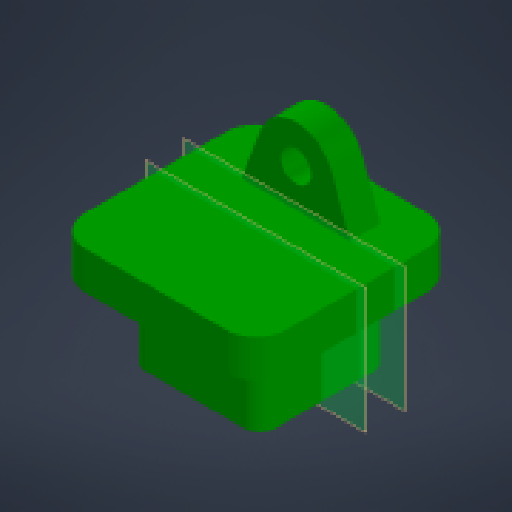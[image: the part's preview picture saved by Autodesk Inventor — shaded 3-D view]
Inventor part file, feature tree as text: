
AUTODESK INVENTOR PART (.ipt)
format: ipt  version: 2024 (Build 280153000, 153)  size: 190,464 bytes
history: native  units: mm
features: other x8, reference x8, extrude x3, sketch x3, fillet x2
ambient origin geometry x8: Origin, YZ Plane, XZ Plane, XY Plane, X Axis, Y Axis, Z Axis, Center Point
bodies: Body1 (feature_tree)
feature tree (24):
  other  "Твердое тело1"
  extrude  "Выдавливание1"  Depth=2.0mm
  extrude  "Выдавливание2"  Depth=10.0mm TaperAngle=0.0deg
  fillet  "Сопряжение1"  Radius=5.0mm
  fillet  "Сопряжение2"  Radius=2.0mm
  other  "РабПлоскость2"
  extrude  "Выдавливание3"  Depth=4.0mm
  sketch  "Эскиз1"
  reference  "Ссылка1"
  reference  "Ссылка2"
  reference  "Ссылка3"
  reference  "Ссылка4"
  sketch  "Эскиз2"
  reference  "Ссылка5"
  reference  "Ссылка6"
  reference  "Ссылка7"
  reference  "Ссылка8"
  other  "РабПлоскость1"
  sketch  "Эскиз3"
  parser-record x1  (decoder bookkeeping rows leaked as tree rows — omitted from the tree; the rows remain in map.json)
  other  "main_assembly.iam"
  other  "base_assembly:1"
  other  "shock_absorber_holder_down_200:1"
  other  "shock_absorber_holder_up:3"
note: 1 file-system path scrubbed to <path> (originals preserved in map.json)
